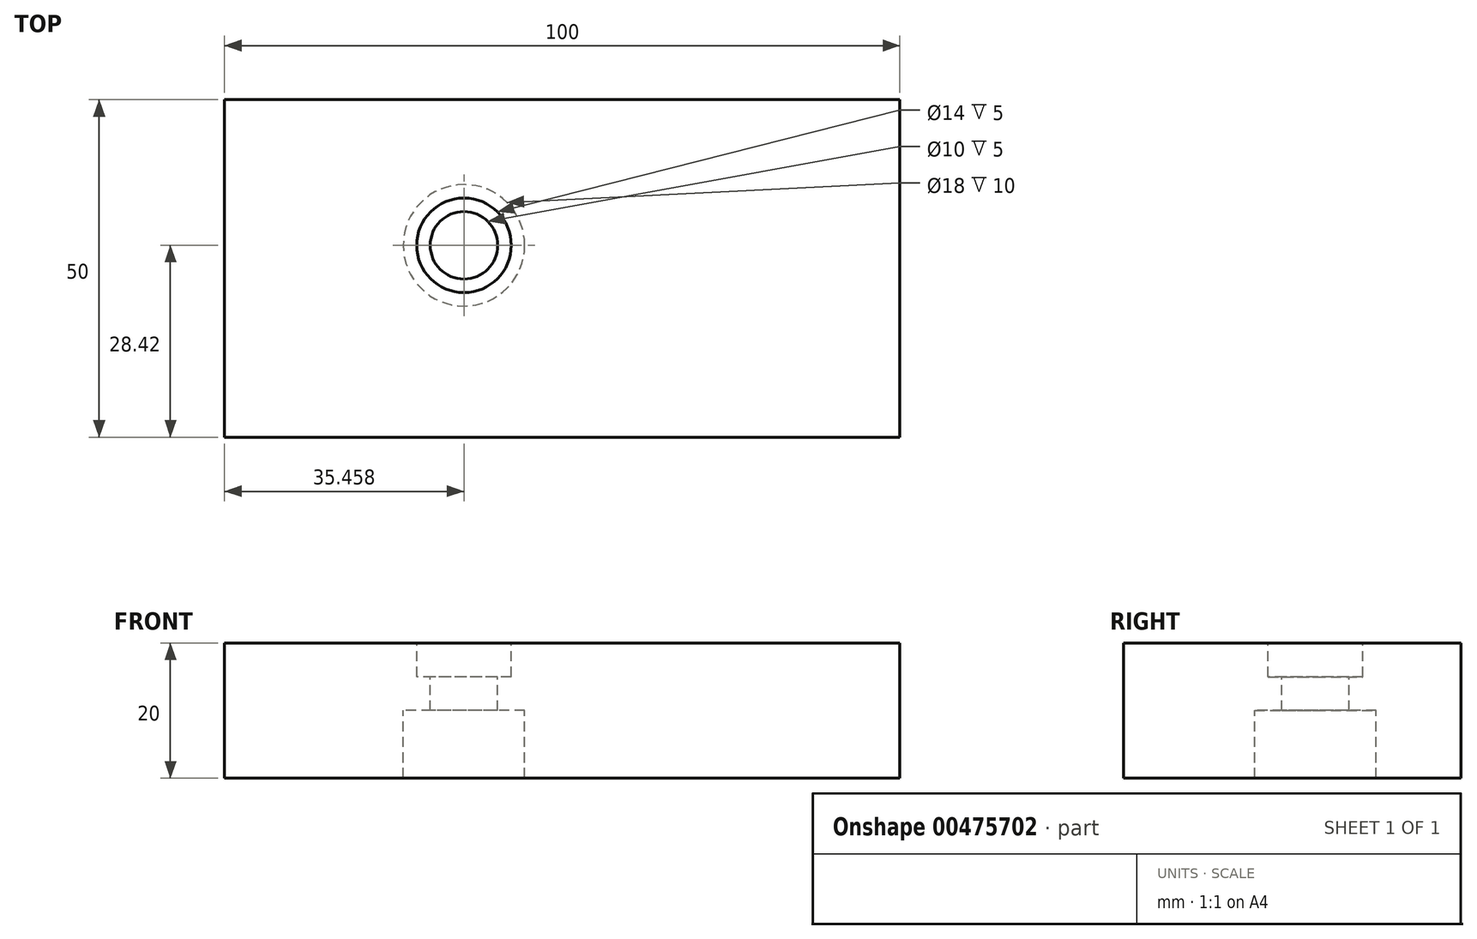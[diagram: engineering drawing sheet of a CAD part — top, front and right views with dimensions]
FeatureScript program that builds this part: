
annotation { "Feature Type Name" : "Feature", "Feature Type Description" : "" }
export const myFeature = defineFeature(function(context is Context, id is Id, definition is map)
    precondition{}
    {
        {
            var Q0;
            Q0=qCreatedBy(makeId("Top.planeOp"),FACE);
            var sketch = newSketch(context, id + "F0", { "sketchPlane" : qUnion([Q0])});
            skLineSegment(sketch, "E0.bottom", {"start": v(-45.54, 21.58) * mm, "end": v(54.46, 21.58) * mm});
            skLineSegment(sketch, "E0.top", {"start": v(-45.54, -28.42) * mm, "end": v(54.46, -28.42) * mm});
            skLineSegment(sketch, "E0.left", {"start": v(-45.54, 21.58) * mm, "end": v(-45.54, -28.42) * mm});
            skLineSegment(sketch, "E0.right", {"start": v(54.46, 21.58) * mm, "end": v(54.46, -28.42) * mm});
            skSolve(sketch);
        }
        {
            var Q0;
            Q0 = qSketchRegion(id + "F0", true);
            extrude(context, id + "F1", {"entities" : qUnion([Q0]), "depth" : 20 * mm});
        }
        {
            var Q0;
            Q0=makeQuery(id+"F1.opExtrude","CAP_FACE",FACE,{"disambiguationData":[OSD([sQuery(id+"F0.wireOp",EDGE,"E0.bottom"),sQuery(id+"F0.wireOp",EDGE,"E0.top"),sQuery(id+"F0.wireOp",EDGE,"E0.left"),sQuery(id+"F0.wireOp",EDGE,"E0.right")])],"isStart":false});
            var sketch = newSketch(context, id + "F2", { "sketchPlane" : qUnion([Q0])});
            skCircle(sketch, "E1", {"center": v(-10.08, 0) * mm, "radius": 7 * mm});
            skSolve(sketch);
        }
        {
            var Q0;
            Q0 = qSketchRegion(id + "F2", true);
            extrude(context, id + "F3", {"entities" : qUnion([Q0]), "operationType" : NewBodyOperationType.REMOVE, "oppositeDirection" : true, "depth" : 5 * mm});
        }
        {
            var Q0;
            Q0=makeQuery(id+"F3.boolean.opBoolean","COPY",FACE,{"derivedFrom":makeQuery(id+"F3.opExtrude","CAP_FACE",FACE,{"disambiguationData":[OSD([sQuery(id+"F2.wireOp",EDGE,"E1")])],"isStart":false})});
            var sketch = newSketch(context, id + "F4", { "sketchPlane" : qUnion([Q0])});
            skCircle(sketch, "E2", {"center": v(-10.08, 0) * mm, "radius": 5 * mm});
            skSolve(sketch);
        }
        {
            var Q0;
            Q0 = qSketchRegion(id + "F4", true);
            extrude(context, id + "F5", {"entities" : qUnion([Q0]), "operationType" : NewBodyOperationType.REMOVE, "oppositeDirection" : true, "depth" : 5 * mm});
        }
        {
            var Q0;
            Q0=makeQuery(id+"F5.boolean.opBoolean","COPY",FACE,{"derivedFrom":makeQuery(id+"F5.opExtrude","CAP_FACE",FACE,{"disambiguationData":[OSD([sQuery(id+"F4.wireOp",EDGE,"E2")])],"isStart":false})});
            var sketch = newSketch(context, id + "F6", { "sketchPlane" : qUnion([Q0])});
            skCircle(sketch, "E3", {"center": v(-10.08, 0) * mm, "radius": 9 * mm});
            skSolve(sketch);
        }
        {
            var Q0;
            Q0 = qSketchRegion(id + "F6", true);
            extrude(context, id + "F7", {"entities" : qUnion([Q0]), "operationType" : NewBodyOperationType.REMOVE, "oppositeDirection" : true, "depth" : 25 * mm});
        }
    });
